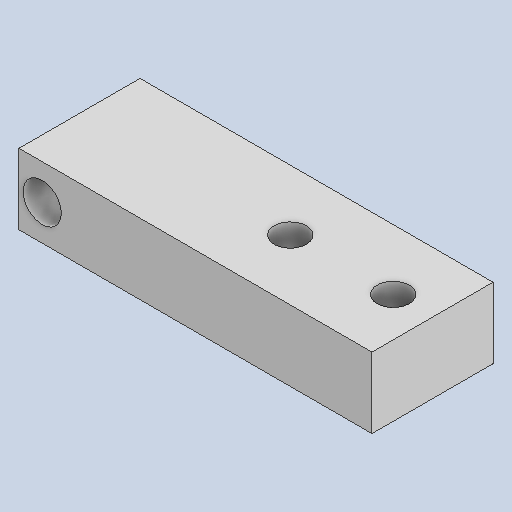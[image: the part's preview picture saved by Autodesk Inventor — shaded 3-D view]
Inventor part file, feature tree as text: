
AUTODESK INVENTOR PART (.ipt)
format: ipt  version: 2024.3 (Build 283343000, 343)  size: 101,376 bytes
history: native  units: mm
features: other x3, sketch x2
ambient origin geometry x8: Origin, YZ Plane, XZ Plane, XY Plane, X Axis, Y Axis, Z Axis, Center Point
bodies: Solid1 (feature_tree)
feature tree (5):
  other  "dedos.ipt"
  other  "Solid1::dedos.ipt"
  other  "TaggingFeature1"
  sketch  "Sketch1"  dims[d0=10.0mm]
  sketch  "Sketch2"
